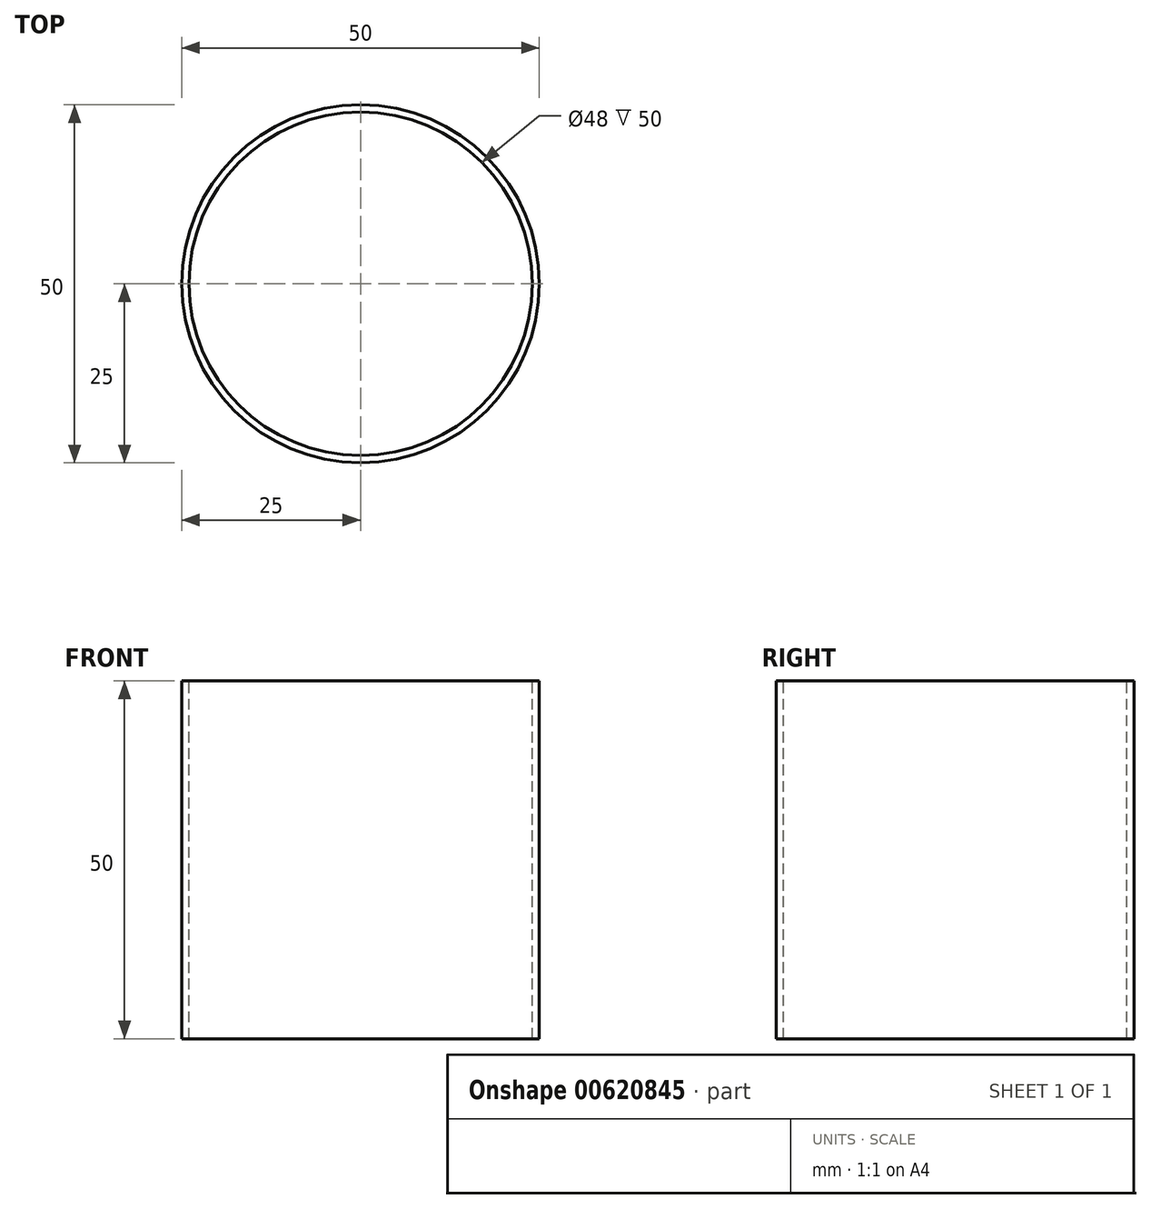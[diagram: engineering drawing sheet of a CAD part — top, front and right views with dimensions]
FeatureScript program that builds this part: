
annotation { "Feature Type Name" : "Feature", "Feature Type Description" : "" }
export const myFeature = defineFeature(function(context is Context, id is Id, definition is map)
    precondition{}
    {
        {
            var Q0;
            Q0=qCreatedBy(makeId("Top.planeOp"),FACE);
            var sketch = newSketch(context, id + "F0", { "sketchPlane" : qUnion([Q0])});
            skCircle(sketch, "E0", {"center": v(0, 0) * mm, "radius": 25 * mm});
            skCircle(sketch, "E1", {"center": v(0, 0) * mm, "radius": 24 * mm});
            skLineSegment(sketch, "E2", {"start": v(-24, 0) * mm, "end": v(24, 0) * mm});
            skSolve(sketch);
        }
        {
            var Q0;
            Q0=makeQuery(id+"F0.imprint","IMPRINT",FACE,{"disambiguationData":[TD([[makeQuery(id+"F0.imprint","IMPRINT",EDGE,{"derivedFrom":sQuery(id+"F0.wireOp",EDGE,"E0")}),1.0]])]});
            var Q1;
            Q1=sQuery(id+"F0.wireOp",EDGE,"E2");
            extrude(context, id + "F1", {"entities" : qUnion([Q0]), "surfaceEntities" : qUnion([Q1]), "oppositeDirection" : true, "depth" : 25 * mm, "offsetDistance" : 25 * mm, "hasSecondDirection" : true, "secondDirectionOppositeDirection" : false, "secondDirectionDepth" : 25 * mm});
        }
    });
